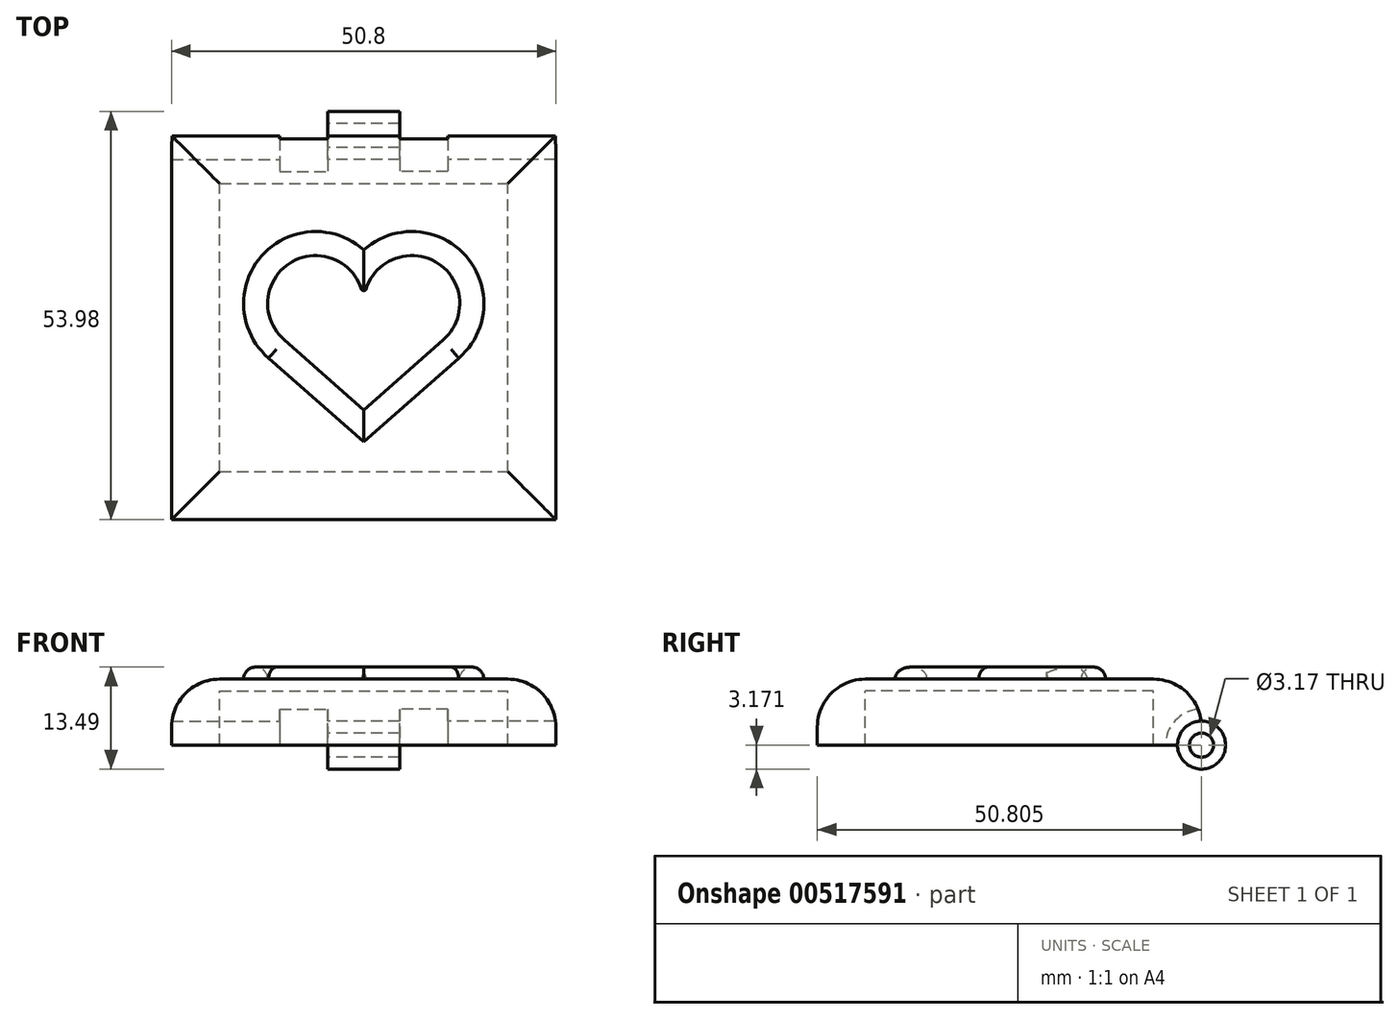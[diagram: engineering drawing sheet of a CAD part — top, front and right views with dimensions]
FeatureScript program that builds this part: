
annotation { "Feature Type Name" : "Feature", "Feature Type Description" : "" }
export const myFeature = defineFeature(function(context is Context, id is Id, definition is map)
    precondition{}
    {
        {
            var Q0;
            Q0=qCreatedBy(makeId("Top.planeOp"),FACE);
            var sketch = newSketch(context, id + "F0", { "sketchPlane" : qUnion([Q0])});
            skArc(sketch, "E0", {"start": v(0, 7.1) * mm, "mid": v(-13.5, 6.29) * mm, "end": v(-12.57, -7.21) * mm});
            skArc(sketch, "E1", {"start": v(0, 7.1) * mm, "mid": v(13.5, 6.29) * mm, "end": v(12.57, -7.21) * mm});
            skLineSegment(sketch, "E2", {"start": v(-12.57, -7.21) * mm, "end": v(0, -18.3) * mm});
            skLineSegment(sketch, "E3", {"start": v(0, -18.3) * mm, "end": v(12.57, -7.21) * mm});
            skArc(sketch, "E4", {"start": v(0, 0) * mm, "mid": v(-9, 5.77) * mm, "end": v(-10.5, -4.8) * mm});
            skArc(sketch, "E5", {"start": v(0, 0) * mm, "mid": v(9, 5.77) * mm, "end": v(10.49, -4.82) * mm});
            skLineSegment(sketch, "E6", {"start": v(10.49, -4.82) * mm, "end": v(0, -14.07) * mm});
            skLineSegment(sketch, "E7", {"start": v(0, -14.07) * mm, "end": v(-10.47, -4.83) * mm});
            skLineSegment(sketch, "E8", {"start": v(-10.47, -4.83) * mm, "end": v(-10.5, -4.8) * mm});
            skSolve(sketch);
        }
        {
            var Q0;
            Q0=makeQuery(id+"F0.imprint","IMPRINT",FACE,{"disambiguationData":[TD([[makeQuery(id+"F0.imprint","IMPRINT",EDGE,{"derivedFrom":sQuery(id+"F0.wireOp",EDGE,"E0")}),1.0]])]});
            extrude(context, id + "F1", {"entities" : qUnion([Q0]), "depth" : 6.35 * mm});
        }
        {
            var Q0;
            Q0=makeQuery(id+"F1.opExtrude","CAP_FACE",FACE,{"disambiguationData":[OSD([sQuery(id+"F0.wireOp",EDGE,"E0"),sQuery(id+"F0.wireOp",EDGE,"E1"),sQuery(id+"F0.wireOp",EDGE,"E2"),sQuery(id+"F0.wireOp",EDGE,"E3")])],"isStart":false});
            var Q1;
            Q1=makeQuery(id+"F1.opExtrude","CAP_FACE",FACE,{"disambiguationData":[OSD([sQuery(id+"F0.wireOp",EDGE,"E0"),sQuery(id+"F0.wireOp",EDGE,"E1"),sQuery(id+"F0.wireOp",EDGE,"E2"),sQuery(id+"F0.wireOp",EDGE,"E3")])],"isStart":true});
            fillet(context, id + "F2", {"entities" : qUnion([Q0, Q1]), "radius" : 1.57 * mm, "tangentPropagation" : true, "allowEdgeOverflow" : false});
        }
        {
            var Q0;
            Q0=makeQuery(id+"F2.opFillet","BLEND_EDGE",EDGE,{"blendedFrom":[makeQuery(id+"F1.opExtrude","CAP_EDGE",EDGE,{"disambiguationData":[OSD([sQuery(id+"F0.wireOp",EDGE,"E0")])],"isStart":false}),makeQuery(id+"F1.opExtrude","CAP_EDGE",EDGE,{"disambiguationData":[OSD([sQuery(id+"F0.wireOp",EDGE,"E2")])],"isStart":false})],"blendedInto":[]});
            var Q1;
            Q1=makeQuery(id+"F2.opFillet","BLEND_EDGE",EDGE,{"blendedFrom":[makeQuery(id+"F1.opExtrude","CAP_EDGE",EDGE,{"disambiguationData":[OSD([sQuery(id+"F0.wireOp",EDGE,"E1")])],"isStart":false}),makeQuery(id+"F1.opExtrude","CAP_EDGE",EDGE,{"disambiguationData":[OSD([sQuery(id+"F0.wireOp",EDGE,"E3")])],"isStart":false})],"blendedInto":[]});
            var Q2;
            Q2=makeQuery(id+"F1.opExtrude","SWEPT_EDGE",EDGE,{"disambiguationData":[OSD([sQuery(id+"F0.wireOp",EDGE,"E0"),sQuery(id+"F0.wireOp",EDGE,"E2")])]});
            var Q3;
            Q3=makeQuery(id+"F1.opExtrude","SWEPT_EDGE",EDGE,{"disambiguationData":[OSD([sQuery(id+"F0.wireOp",EDGE,"E1"),sQuery(id+"F0.wireOp",EDGE,"E3")])]});
            var Q4;
            Q4=makeQuery(id+"F2.opFillet","BLEND_EDGE",EDGE,{"blendedFrom":[makeQuery(id+"F1.opExtrude","CAP_EDGE",EDGE,{"disambiguationData":[OSD([sQuery(id+"F0.wireOp",EDGE,"E0")])],"isStart":true}),makeQuery(id+"F1.opExtrude","CAP_EDGE",EDGE,{"disambiguationData":[OSD([sQuery(id+"F0.wireOp",EDGE,"E2")])],"isStart":true})],"blendedInto":[]});
            var Q5;
            Q5=makeQuery(id+"F2.opFillet","BLEND_EDGE",EDGE,{"blendedFrom":[makeQuery(id+"F1.opExtrude","CAP_EDGE",EDGE,{"disambiguationData":[OSD([sQuery(id+"F0.wireOp",EDGE,"E1")])],"isStart":true}),makeQuery(id+"F1.opExtrude","CAP_EDGE",EDGE,{"disambiguationData":[OSD([sQuery(id+"F0.wireOp",EDGE,"E3")])],"isStart":true})],"blendedInto":[]});
            var Q6;
            Q6=makeQuery(id+"F2.opFillet","BLEND_EDGE",EDGE,{"blendedFrom":[makeQuery(id+"F1.opExtrude","CAP_EDGE",EDGE,{"disambiguationData":[OSD([sQuery(id+"F0.wireOp",EDGE,"E5")])],"isStart":false}),makeQuery(id+"F1.opExtrude","CAP_EDGE",EDGE,{"disambiguationData":[OSD([sQuery(id+"F0.wireOp",EDGE,"E6")])],"isStart":false})],"blendedInto":[]});
            var Q7;
            Q7=makeQuery(id+"F2.opFillet","BLEND_EDGE",EDGE,{"blendedFrom":[makeQuery(id+"F1.opExtrude","CAP_EDGE",EDGE,{"disambiguationData":[OSD([sQuery(id+"F0.wireOp",EDGE,"E4")])],"isStart":false}),makeQuery(id+"F1.opExtrude","CAP_EDGE",EDGE,{"disambiguationData":[OSD([sQuery(id+"F0.wireOp",EDGE,"E8")])],"isStart":false})],"blendedInto":[]});
            var Q8;
            Q8=makeQuery(id+"F1.opExtrude","SWEPT_EDGE",EDGE,{"disambiguationData":[OSD([sQuery(id+"F0.wireOp",EDGE,"E5"),sQuery(id+"F0.wireOp",EDGE,"E6")])]});
            var Q9;
            Q9=makeQuery(id+"F2.opFillet","BLEND_EDGE",EDGE,{"blendedFrom":[makeQuery(id+"F1.opExtrude","CAP_EDGE",EDGE,{"disambiguationData":[OSD([sQuery(id+"F0.wireOp",EDGE,"E5")])],"isStart":true}),makeQuery(id+"F1.opExtrude","CAP_EDGE",EDGE,{"disambiguationData":[OSD([sQuery(id+"F0.wireOp",EDGE,"E6")])],"isStart":true})],"blendedInto":[]});
            var Q10;
            Q10=makeQuery(id+"F2.opFillet","BLEND_EDGE",EDGE,{"blendedFrom":[makeQuery(id+"F1.opExtrude","CAP_EDGE",EDGE,{"disambiguationData":[OSD([sQuery(id+"F0.wireOp",EDGE,"E7")])],"isStart":true}),makeQuery(id+"F1.opExtrude","CAP_EDGE",EDGE,{"disambiguationData":[OSD([sQuery(id+"F0.wireOp",EDGE,"E8")])],"isStart":true})],"blendedInto":[]});
            var Q11;
            Q11=makeQuery(id+"F1.opExtrude","SWEPT_EDGE",EDGE,{"disambiguationData":[OSD([sQuery(id+"F0.wireOp",EDGE,"E7"),sQuery(id+"F0.wireOp",EDGE,"E8")])]});
            fillet(context, id + "F3", {"entities" : qUnion([Q0, Q1, Q2, Q3, Q4, Q5, Q6, Q7, Q8, Q9, Q10, Q11]), "radius" : 2.54 * mm, "tangentPropagation" : true, "allowEdgeOverflow" : false});
        }
        {
            var Q0;
            Q0=makeQuery(id+"F1.opExtrude","SWEPT_EDGE",EDGE,{"disambiguationData":[OSD([sQuery(id+"F0.wireOp",EDGE,"E4"),sQuery(id+"F0.wireOp",EDGE,"E5")])]});
            fillet(context, id + "F4", {"entities" : qUnion([Q0]), "radius" : 0.32 * mm, "tangentPropagation" : true, "allowEdgeOverflow" : false});
        }
        {
            var Q0;
            Q0=qCreatedBy(makeId("Top.planeOp"),FACE);
            var sketch = newSketch(context, id + "F5", { "sketchPlane" : qUnion([Q0])});
            skLineSegment(sketch, "E9.bottom", {"start": v(-25.4, -28.57) * mm, "end": v(25.4, -28.57) * mm});
            skLineSegment(sketch, "E9.top", {"start": v(-25.4, 22.23) * mm, "end": v(25.4, 22.23) * mm});
            skLineSegment(sketch, "E9.left", {"start": v(-25.4, -28.57) * mm, "end": v(-25.4, 22.23) * mm});
            skLineSegment(sketch, "E9.right", {"start": v(25.4, -28.57) * mm, "end": v(25.4, 22.23) * mm});
            skPoint(sketch, "E9.middle", {"position": v(0, 3.18) * mm});
            skSolve(sketch);
        }
        {
            var Q0;
            Q0 = qSketchRegion(id + "F5", true);
            extrude(context, id + "F6", {"entities" : qUnion([Q0]), "operationType" : NewBodyOperationType.ADD, "oppositeDirection" : true, "depth" : 12.7 * mm, "offsetDistance" : 25.4 * mm, "hasSecondDirection" : true, "secondDirectionOppositeDirection" : false, "secondDirectionDepth" : 4.76 * mm});
        }
        {
            var Q0;
            Q0=makeQuery(id+"F6.opExtrude","CAP_EDGE",EDGE,{"disambiguationData":[OSD([sQuery(id+"F5.wireOp",EDGE,"E9.bottom")])],"isStart":true});
            var Q1;
            Q1=makeQuery(id+"F6.opExtrude","CAP_EDGE",EDGE,{"disambiguationData":[OSD([sQuery(id+"F5.wireOp",EDGE,"E9.right")])],"isStart":true});
            var Q2;
            Q2=makeQuery(id+"F6.opExtrude","CAP_EDGE",EDGE,{"disambiguationData":[OSD([sQuery(id+"F5.wireOp",EDGE,"E9.top")])],"isStart":true});
            var Q3;
            Q3=makeQuery(id+"F6.opExtrude","CAP_EDGE",EDGE,{"disambiguationData":[OSD([sQuery(id+"F5.wireOp",EDGE,"E9.left")])],"isStart":true});
            var Q4;
            Q4=makeQuery(id+"F6.opExtrude","CAP_FACE",FACE,{"disambiguationData":[OSD([sQuery(id+"F5.wireOp",EDGE,"E9.bottom"),sQuery(id+"F5.wireOp",EDGE,"E9.top"),sQuery(id+"F5.wireOp",EDGE,"E9.left"),sQuery(id+"F5.wireOp",EDGE,"E9.right")])],"isStart":false});
            fillet(context, id + "F7", {"entities" : qUnion([Q0, Q1, Q2, Q3, Q4]), "radius" : 6.35 * mm, "tangentPropagation" : true, "allowEdgeOverflow" : false});
        }
        {
            var Q0;
            Q0=qCreatedBy(makeId("Front.planeOp"),FACE);
            var sketch = newSketch(context, id + "F8", { "sketchPlane" : qUnion([Q0])});
            skLineSegment(sketch, "E10.bottom", {"start": v(-26.07, -3.97) * mm, "end": v(50.6, -3.97) * mm});
            skLineSegment(sketch, "E10.top", {"start": v(-26.07, -18.23) * mm, "end": v(50.6, -18.23) * mm});
            skLineSegment(sketch, "E10.left", {"start": v(-26.07, -3.97) * mm, "end": v(-26.07, -18.23) * mm});
            skLineSegment(sketch, "E10.right", {"start": v(50.6, -3.97) * mm, "end": v(50.6, -18.23) * mm});
            skSolve(sketch);
        }
        {
            var Q0;
            Q0 = qSketchRegion(id + "F8", true);
            extrude(context, id + "F9", {"entities" : qUnion([Q0]), "operationType" : NewBodyOperationType.REMOVE, "endBound" : BoundingType.SYMMETRIC, "oppositeDirection" : true, "depth" : 63.5 * mm, "offsetDistance" : 25.4 * mm});
        }
        {
            var Q0;
            Q0=makeQuery(id+"F9.boolean.opBoolean","COPY",FACE,{"derivedFrom":makeQuery(id+"F9.opExtrude","SWEPT_FACE",FACE,{"disambiguationData":[OSD([sQuery(id+"F8.wireOp",EDGE,"E10.bottom")])]})});
            shell(context, id + "F10", {"entities" : qUnion([Q0]), "thickness" : 6.35 * mm});
        }
        {
            var Q0;
            Q0=qCreatedBy(makeId("Right.planeOp"),FACE);
            var sketch = newSketch(context, id + "F11", { "sketchPlane" : qUnion([Q0])});
            skCircle(sketch, "E11", {"center": v(22.23, -3.97) * mm, "radius": 3.18 * mm});
            skCircle(sketch, "E12", {"center": v(22.23, -3.97) * mm, "radius": 1.59 * mm});
            skSolve(sketch);
        }
        {
            var Q0;
            Q0 = qSketchRegion(id + "F11", true);
            extrude(context, id + "F12", {"entities" : qUnion([Q0]), "operationType" : NewBodyOperationType.ADD, "endBound" : BoundingType.SYMMETRIC, "depth" : 25.4 * mm, "offsetDistance" : 25.4 * mm});
        }
        {
            var Q0;
            Q0=makeQuery(id+"F11.imprint","IMPRINT",FACE,{"disambiguationData":[TD([[makeQuery(id+"F11.imprint","IMPRINT",EDGE,{"derivedFrom":sQuery(id+"F11.wireOp",EDGE,"E12")}),1.0]])]});
            extrude(context, id + "F13", {"entities" : qUnion([Q0]), "operationType" : NewBodyOperationType.REMOVE, "endBound" : BoundingType.SYMMETRIC, "oppositeDirection" : true, "depth" : 50.8 * mm, "offsetDistance" : 25.4 * mm});
        }
        {
            var Q0;
            Q0=makeQuery(id+"F12.opExtrude","CAP_FACE",FACE,{"disambiguationData":[OSD([sQuery(id+"F11.wireOp",EDGE,"E11"),sQuery(id+"F11.wireOp",EDGE,"E12")])],"isStart":false});
            extrude(context, id + "F14", {"entities" : qUnion([Q0]), "operationType" : NewBodyOperationType.REMOVE, "oppositeDirection" : true, "depth" : 6.35 * mm, "offsetDistance" : 25.4 * mm});
        }
        {
            var Q0;
            Q0=makeQuery(id+"F12.opExtrude","CAP_FACE",FACE,{"disambiguationData":[OSD([sQuery(id+"F11.wireOp",EDGE,"E11"),sQuery(id+"F11.wireOp",EDGE,"E12")])],"isStart":true});
            extrude(context, id + "F15", {"entities" : qUnion([Q0]), "operationType" : NewBodyOperationType.REMOVE, "oppositeDirection" : true, "depth" : 6.35 * mm, "offsetDistance" : 25.4 * mm});
        }
        {
            var Q0;
            Q0=makeQuery(id+"F15.boolean.opBoolean","COPY",FACE,{"derivedFrom":makeQuery(id+"F15.opExtrude","CAP_FACE",FACE,{"disambiguationData":[OSD([sQuery(id+"F11.wireOp",EDGE,"E11"),sQuery(id+"F11.wireOp",EDGE,"E12")])],"isStart":false})});
            extrude(context, id + "F16", {"entities" : qUnion([Q0]), "operationType" : NewBodyOperationType.REMOVE, "oppositeDirection" : true, "depth" : 1.59 * mm, "offsetDistance" : 25.4 * mm});
        }
        {
            var Q0;
            Q0=makeQuery(id+"F14.boolean.opBoolean","COPY",FACE,{"derivedFrom":makeQuery(id+"F14.opExtrude","CAP_FACE",FACE,{"disambiguationData":[OSD([sQuery(id+"F11.wireOp",EDGE,"E11"),sQuery(id+"F11.wireOp",EDGE,"E12")])],"isStart":false})});
            extrude(context, id + "F17", {"entities" : qUnion([Q0]), "operationType" : NewBodyOperationType.REMOVE, "oppositeDirection" : true, "depth" : 1.59 * mm, "offsetDistance" : 25.4 * mm});
        }
        {
            var Q0;
            Q0 = qSketchRegion(id + "F11", true);
            extrude(context, id + "F18", {"entities" : qUnion([Q0]), "operationType" : NewBodyOperationType.REMOVE, "oppositeDirection" : true, "depth" : 25.4 * mm, "offsetDistance" : 25.4 * mm, "hasSecondDirection" : true, "secondDirectionOppositeDirection" : true, "secondDirectionDepth" : 4.76 * mm});
        }
        {
            var Q0;
            Q0=makeQuery(id+"F10.opShell","OFFSET_FACE",FACE,{"disambiguationData":[OSD([sQuery(id+"F5.wireOp",EDGE,"E9.bottom"),sQuery(id+"F5.wireOp",EDGE,"E9.top"),sQuery(id+"F5.wireOp",EDGE,"E9.left"),sQuery(id+"F5.wireOp",EDGE,"E9.right")])]});
            extrude(context, id + "F19", {"entities" : qUnion([Q0]), "operationType" : NewBodyOperationType.REMOVE, "oppositeDirection" : true, "depth" : 4.76 * mm, "offsetDistance" : 25.4 * mm});
        }
        {
            var Q0;
            Q0 = qSketchRegion(id + "F11", true);
            extrude(context, id + "F20", {"entities" : qUnion([Q0]), "operationType" : NewBodyOperationType.REMOVE, "depth" : 25.4 * mm, "offsetDistance" : 25.4 * mm, "hasSecondDirection" : true, "secondDirectionOppositeDirection" : false, "secondDirectionDepth" : 4.76 * mm});
        }
        {
            var Q0;
            Q0=qCreatedBy(makeId("Right.planeOp"),FACE);
            var sketch = newSketch(context, id + "F21", { "sketchPlane" : qUnion([Q0])});
            skCircle(sketch, "E13", {"center": v(22.23, -3.97) * mm, "radius": 4.76 * mm});
            skSolve(sketch);
        }
        {
            var Q0;
            Q0 = qSketchRegion(id + "F21", true);
            extrude(context, id + "F22", {"entities" : qUnion([Q0]), "operationType" : NewBodyOperationType.REMOVE, "oppositeDirection" : true, "depth" : 11.1 * mm, "offsetDistance" : 25.4 * mm, "hasSecondDirection" : true, "secondDirectionOppositeDirection" : true, "secondDirectionDepth" : 4.76 * mm});
        }
        {
            var Q0;
            Q0 = qSketchRegion(id + "F21", true);
            extrude(context, id + "F23", {"entities" : qUnion([Q0]), "operationType" : NewBodyOperationType.REMOVE, "depth" : 11.1 * mm, "offsetDistance" : 25.4 * mm, "hasSecondDirection" : true, "secondDirectionOppositeDirection" : false, "secondDirectionDepth" : 4.76 * mm});
        }
    });
